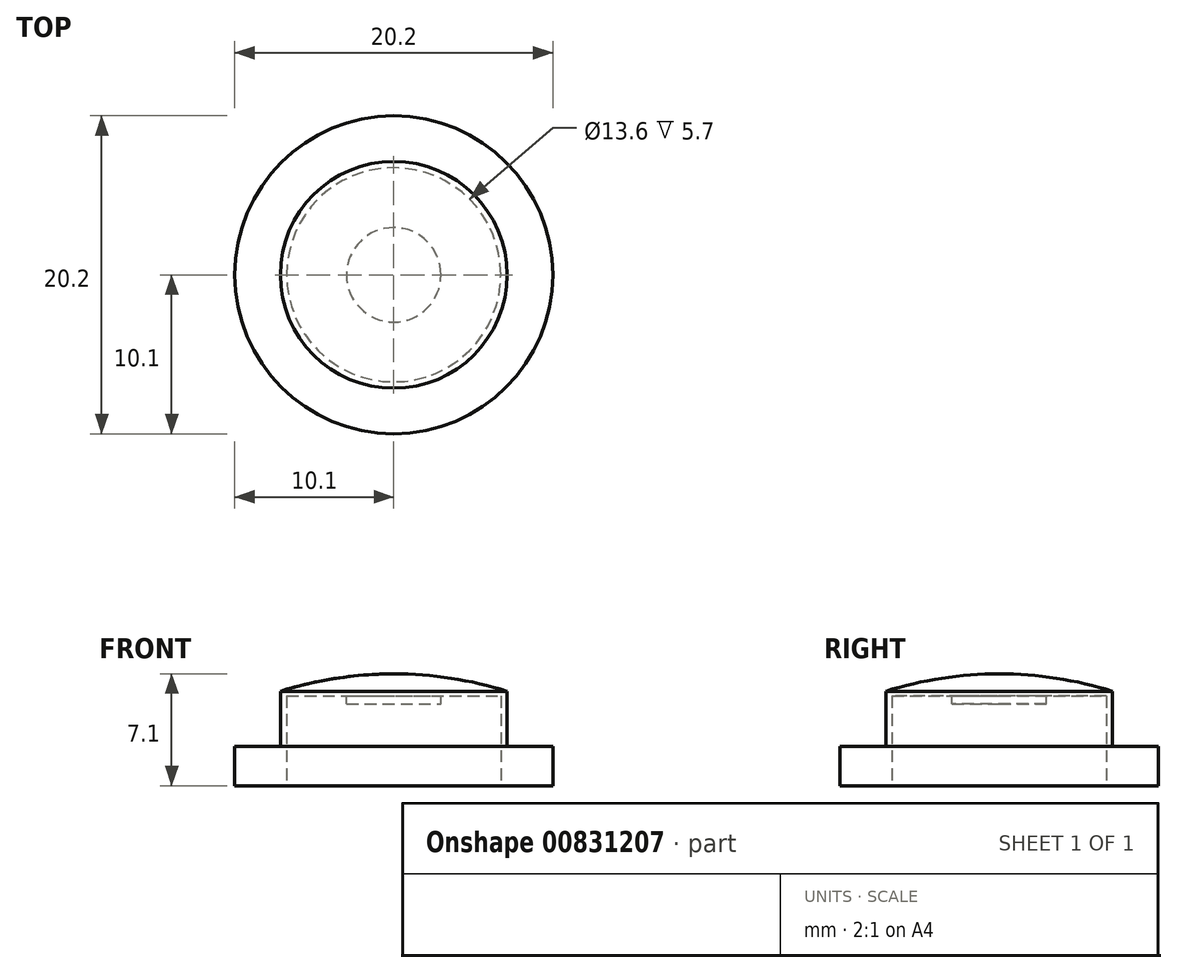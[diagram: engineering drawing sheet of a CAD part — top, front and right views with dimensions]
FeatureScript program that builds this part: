
annotation { "Feature Type Name" : "Feature", "Feature Type Description" : "" }
export const myFeature = defineFeature(function(context is Context, id is Id, definition is map)
    precondition{}
    {
        {
            var Q0;
            Q0=qCreatedBy(makeId("Front.planeOp"),FACE);
            var sketch = newSketch(context, id + "F0", { "sketchPlane" : qUnion([Q0])});
            skLineSegment(sketch, "E0", {"start": v(0, 0) * mm, "end": v(-10.1, 0) * mm});
            skLineSegment(sketch, "E1", {"start": v(-10.1, 0) * mm, "end": v(-10.1, 2.5) * mm});
            skLineSegment(sketch, "E2", {"start": v(-10.1, 2.5) * mm, "end": v(-7.2, 2.5) * mm});
            skLineSegment(sketch, "E3", {"start": v(-7.2, 2.5) * mm, "end": v(-7.2, 6) * mm});
            skArc(sketch, "E4", {"start": v(0, 7.1) * mm, "mid": v(-3.64, 6.82) * mm, "end": v(-7.2, 6) * mm});
            skPoint(sketch, "E5", {"position": v(0, 7.1) * mm});
            skLineSegment(sketch, "E6", {"start": v(0, 7.1) * mm, "end": v(0, 0) * mm});
            skSolve(sketch);
        }
        {
            var Q0;
            Q0 = qSketchRegion(id + "F0", true);
            var Q1;
            Q1=sQuery(id+"F0.wireOp",EDGE,"E6");
            revolve(context, id + "F1", {"surfaceOperationType" : NewSurfaceOperationType.NEW, "entities" : qUnion([Q0]), "axis" : qUnion([Q1]), "revolveType" : RevolveType.FULL});
        }
        {
            var Q0;
            Q0=makeQuery(id+"F1.opRevolve","SWEPT_FACE",FACE,{"disambiguationData":[OSD([sQuery(id+"F0.wireOp",EDGE,"E0")])]});
            var sketch = newSketch(context, id + "F2", { "sketchPlane" : qUnion([Q0])});
            skCircle(sketch, "E7", {"center": v(0, 0) * mm, "radius": 6.8 * mm});
            skSolve(sketch);
        }
        {
            var Q0;
            Q0=makeQuery(id+"F2.imprint","IMPRINT",FACE,{"disambiguationData":[TD([[makeQuery(id+"F2.imprint","IMPRINT",EDGE,{"derivedFrom":sQuery(id+"F2.wireOp",EDGE,"E7")}),1.0]])]});
            extrude(context, id + "F3", {"entities" : qUnion([Q0]), "operationType" : NewBodyOperationType.REMOVE, "oppositeDirection" : true, "depth" : 5.7 * mm, "offsetDistance" : 25 * mm});
        }
        {
            var Q0;
            Q0=makeQuery(id+"F3.boolean.opBoolean","COPY",FACE,{"derivedFrom":makeQuery(id+"F3.opExtrude","CAP_FACE",FACE,{"disambiguationData":[OSD([sQuery(id+"F2.wireOp",EDGE,"E7")])],"isStart":false})});
            var sketch = newSketch(context, id + "F4", { "sketchPlane" : qUnion([Q0])});
            skCircle(sketch, "E8", {"center": v(0, 0) * mm, "radius": 3 * mm});
            skSolve(sketch);
        }
        {
            var Q0;
            Q0=makeQuery(id+"F4.imprint","IMPRINT",FACE,{"disambiguationData":[TD([[makeQuery(id+"F4.imprint","IMPRINT",EDGE,{"derivedFrom":sQuery(id+"F4.wireOp",EDGE,"E8")}),1.0]])]});
            extrude(context, id + "F5", {"entities" : qUnion([Q0]), "operationType" : NewBodyOperationType.ADD, "depth" : 0.5 * mm, "offsetDistance" : 25 * mm});
        }
    });
